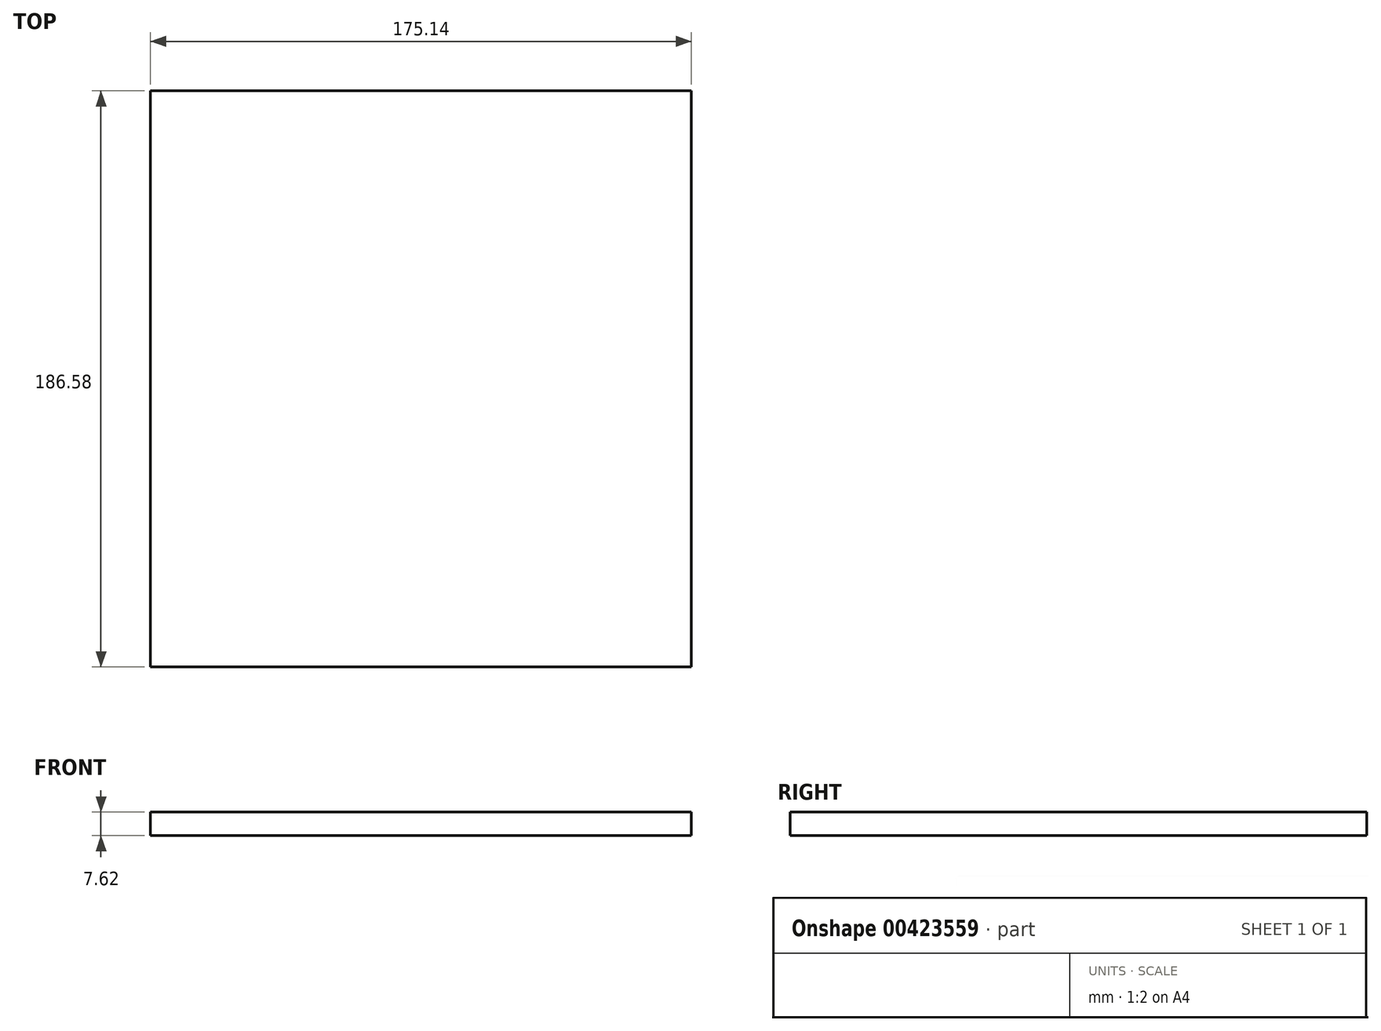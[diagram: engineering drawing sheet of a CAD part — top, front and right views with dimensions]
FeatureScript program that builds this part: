
annotation { "Feature Type Name" : "Feature", "Feature Type Description" : "" }
export const myFeature = defineFeature(function(context is Context, id is Id, definition is map)
    precondition{}
    {
        {
            var Q0;
            Q0=qCreatedBy(makeId("Top.planeOp"),FACE);
            var sketch = newSketch(context, id + "F0", { "sketchPlane" : qUnion([Q0])});
            skLineSegment(sketch, "E0.bottom", {"start": v(-76.03, 55.67) * mm, "end": v(99.1, 55.67) * mm});
            skLineSegment(sketch, "E0.top", {"start": v(-76.03, -130.9) * mm, "end": v(99.1, -130.9) * mm});
            skLineSegment(sketch, "E0.left", {"start": v(-76.03, 55.67) * mm, "end": v(-76.03, -130.9) * mm});
            skLineSegment(sketch, "E0.right", {"start": v(99.1, 55.67) * mm, "end": v(99.1, -130.9) * mm});
            skSolve(sketch);
        }
        {
            var Q0;
            Q0 = qSketchRegion(id + "F0", true);
            extrude(context, id + "F1", {"entities" : qUnion([Q0]), "depth" : 7.62 * mm});
        }
    });
